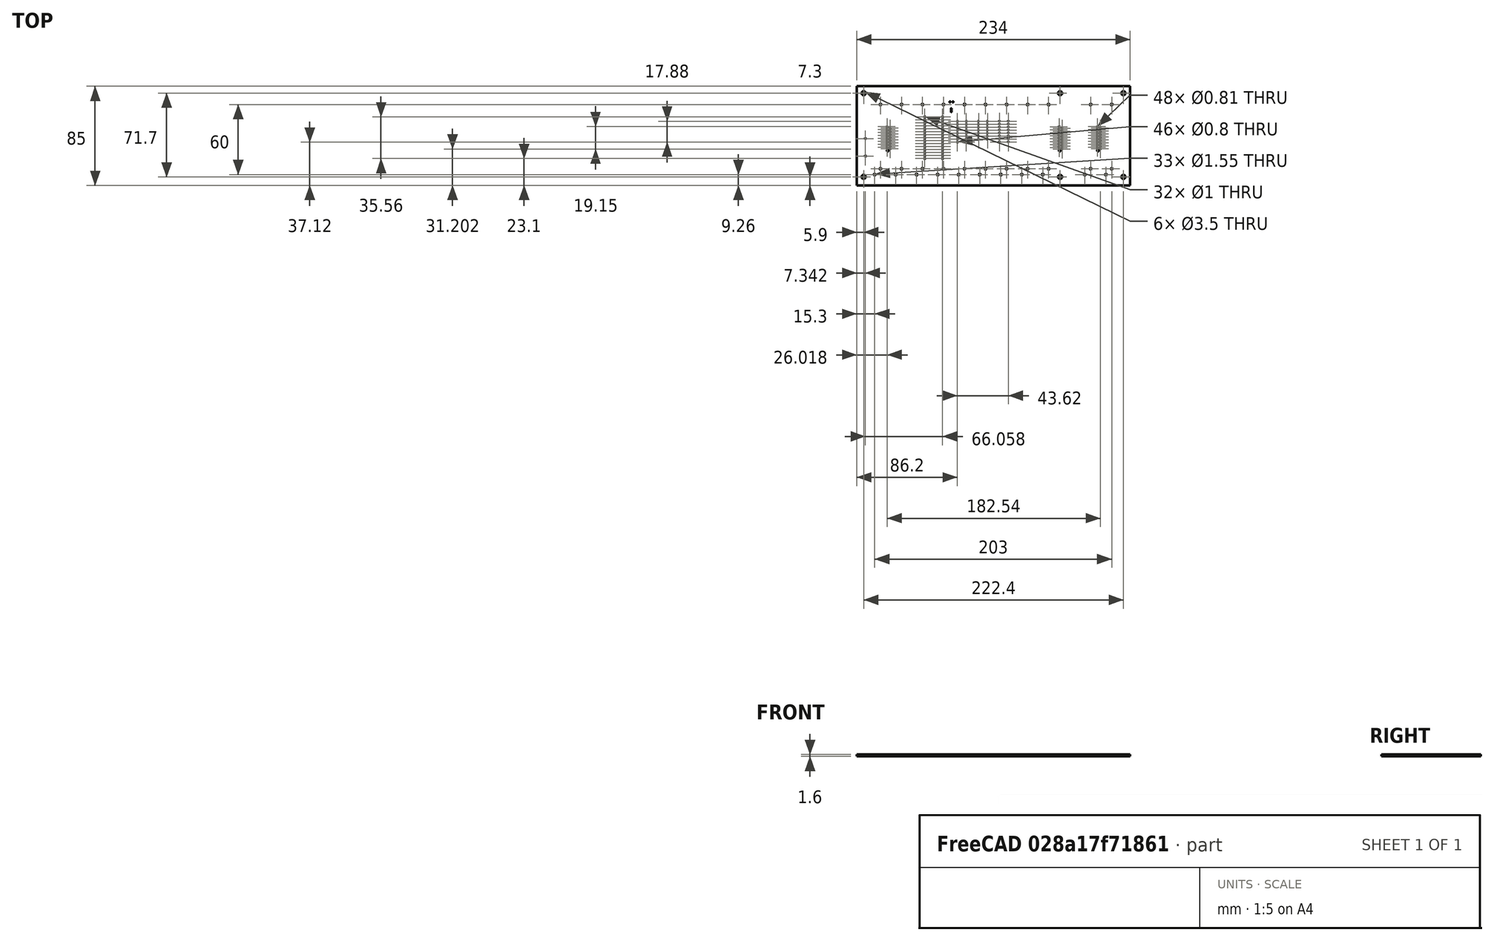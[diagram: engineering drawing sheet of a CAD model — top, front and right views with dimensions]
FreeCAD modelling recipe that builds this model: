
FCSTD DOCUMENT  (FreeCAD 0.20R29603 (Git))
Label: drawbars_pcb
License: All rights reserved
LicenseURL: http://en.wikipedia.org/wiki/All_rights_reserved
objects: App::Part×3, PartDesign::CoordinateSystem×1, Part::Feature×1, Sketcher::SketchObject×1
note: 3 computed .brp shape members not serialized (recipe doc carries the construction recipe); baked Part::Feature solids carry a one-line shape summary decoded from their .brp

FEATURE [PartDesign::CoordinateSystem] Local_CS_3e93
  AttacherType = Attacher::AttachEngine3D
FEATURE [Part::Feature] Pcb_3e93
  Placement = pos=(-31.1,42.1,0) rot=(0,0,1;0rad)
  shape: bbox 234 x 85 x 1.6 mm, 179 faces (baked)
FEATURE [Sketcher::SketchObject] PCB_Sketch_3e93
  FullyConstrained = false
  sketch-geometry (4):
    g0: LineSegment StartX=-0.1 StartY=-84.9 StartZ=0 EndX=-0.1 EndY=0.1 EndZ=0
    g1: LineSegment StartX=-0.1 StartY=0.1 StartZ=0 EndX=233.9 EndY=0.1 EndZ=0
    g2: LineSegment StartX=233.9 StartY=-84.9 StartZ=0 EndX=-0.1 EndY=-84.9 EndZ=0
    g3: LineSegment StartX=233.9 StartY=-84.9 StartZ=0 EndX=233.9 EndY=0.1 EndZ=0
  constraints (4):
    c: Coincident(g0,g2)
    c: Coincident(g0,g1)
    c: Coincident(g2,g3)
    c: Coincident(g1,g3)
FEATURE [App::Part] Board_Geoms_3e93
  Group = -> [Local_CS_3e93,Pcb_3e93,PCB_Sketch_3e93]
  Origin = -> Origin
FEATURE [App::Part] Step_Models_3e93
  Origin = -> Origin002
FEATURE [App::Part] Board_3e93  label="drawbars"
  Group = -> [Board_Geoms_3e93,Step_Models_3e93]
  Origin = -> Origin001
